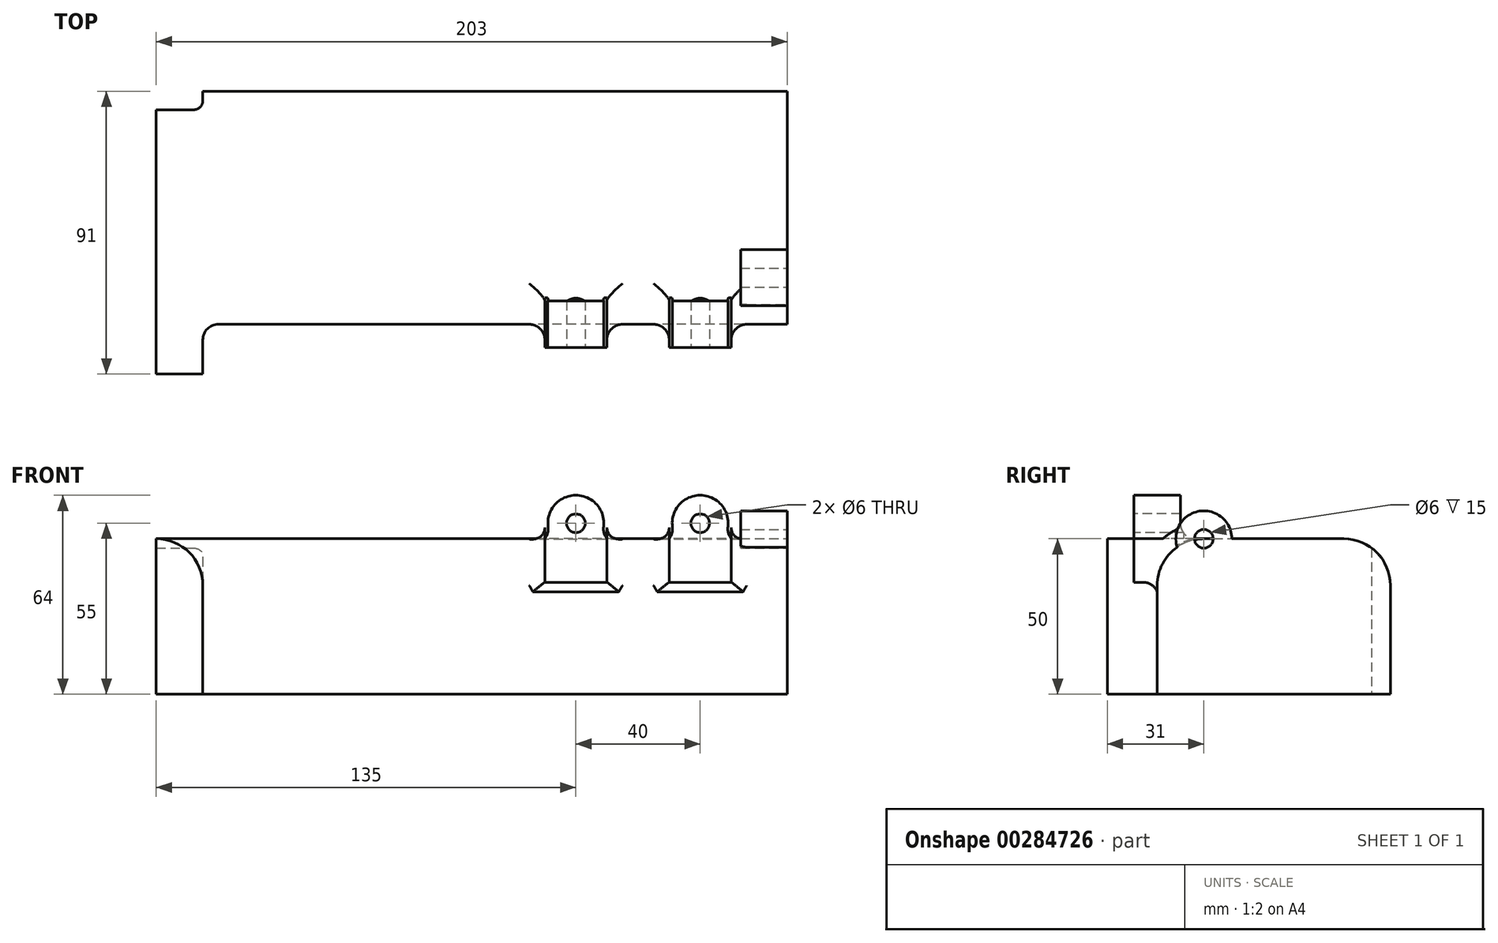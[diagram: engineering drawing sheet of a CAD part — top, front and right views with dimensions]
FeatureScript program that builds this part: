
annotation { "Feature Type Name" : "Feature", "Feature Type Description" : "" }
export const myFeature = defineFeature(function(context is Context, id is Id, definition is map)
    precondition{}
    {
        {
            var Q0;
            Q0=qCreatedBy(makeId("Top.planeOp"),FACE);
            var sketch = newSketch(context, id + "F0", { "sketchPlane" : qUnion([Q0])});
            skLineSegment(sketch, "E0.bottom", {"start": v(4.5, 42.5) * mm, "end": v(-7.5, 42.5) * mm});
            skLineSegment(sketch, "E0.top", {"start": v(7.5, -42.5) * mm, "end": v(-7.5, -42.5) * mm});
            skLineSegment(sketch, "E0.left", {"start": v(7.5, -31.5) * mm, "end": v(7.5, -42.5) * mm});
            skLineSegment(sketch, "E0.right", {"start": v(-7.5, 42.5) * mm, "end": v(-7.5, -42.5) * mm});
            skPoint(sketch, "E0.middle", {"position": v(0, 0) * mm});
            skLineSegment(sketch, "E1", {"start": v(7.5, 45.5) * mm, "end": v(7.5, 48.5) * mm});
            skLineSegment(sketch, "E2", {"start": v(7.5, 48.5) * mm, "end": v(195.5, 48.5) * mm});
            skLineSegment(sketch, "E3", {"start": v(195.5, 48.5) * mm, "end": v(195.5, -26.5) * mm});
            skLineSegment(sketch, "E4", {"start": v(195.5, -26.5) * mm, "end": v(12.5, -26.5) * mm});
            skPoint(sketch, "E5.visualSharp", {"position": v(7.5, 42.5) * mm});
            skArc(sketch, "E5.filletArc", {"start": v(4.5, 42.5) * mm, "mid": v(6.62, 43.38) * mm, "end": v(7.5, 45.5) * mm});
            skArc(sketch, "E6.filletArc", {"start": v(12.5, -26.5) * mm, "mid": v(8.96, -27.96) * mm, "end": v(7.5, -31.5) * mm});
            skSolve(sketch);
        }
        {
            var Q0;
            Q0=qSketchRegion(id+"F0",true);
            extrude(context, id + "F1", {"entities" : qUnion([Q0]), "depth" : 50 * mm});
        }
        {
            var Q0;
            Q0=makeQuery(id+"F1.opExtrude","CAP_EDGE",EDGE,{"disambiguationData":[OSD([sQuery(id+"F0.wireOp",EDGE,"E4")])],"isStart":false});
            var Q1;
            Q1=makeQuery(id+"F1.opExtrude","CAP_EDGE",EDGE,{"disambiguationData":[OSD([sQuery(id+"F0.wireOp",EDGE,"E2")])],"isStart":false});
            fillet(context, id + "F2", {"entities" : qUnion([Q0, Q1]), "radius" : 15 * mm, "tangentPropagation" : true, "allowEdgeOverflow" : false});
        }
        {
            var Q0;
            Q0=makeQuery(id+"F1.opExtrude","CAP_FACE",FACE,{"disambiguationData":[OSD([sQuery(id+"F0.wireOp",EDGE,"E0.bottom"),sQuery(id+"F0.wireOp",EDGE,"E0.top"),sQuery(id+"F0.wireOp",EDGE,"E0.left"),sQuery(id+"F0.wireOp",EDGE,"E0.right"),sQuery(id+"F0.wireOp",EDGE,"E1"),sQuery(id+"F0.wireOp",EDGE,"E2"),sQuery(id+"F0.wireOp",EDGE,"E3"),sQuery(id+"F0.wireOp",EDGE,"E4"),sQuery(id+"F0.wireOp",EDGE,"E5.filletArc"),sQuery(id+"F0.wireOp",EDGE,"E6.filletArc")])],"isStart":false});
            var sketch = newSketch(context, id + "F3", { "sketchPlane" : qUnion([Q0])});
            skLineSegment(sketch, "E7.0.0", {"start": v(195.5, 48.5) * mm, "end": v(180.5, 33.5) * mm, "construction": true});
            skLineSegment(sketch, "E7.0.1", {"start": v(180.5, -11.5) * mm, "end": v(180.5, 33.5) * mm, "construction": true});
            skLineSegment(sketch, "E7.0.2", {"start": v(180.5, -11.5) * mm, "end": v(195.5, -26.5) * mm, "construction": true});
            skLineSegment(sketch, "E7.0.3", {"start": v(195.5, -26.5) * mm, "end": v(195.5, 48.5) * mm, "construction": true});
            skLineSegment(sketch, "E8.0", {"start": v(195.5, -26.5) * mm, "end": v(12.5, -26.5) * mm, "construction": true});
            skLineSegment(sketch, "E9.0", {"start": v(12.5, -11.5) * mm, "end": v(180.5, -11.5) * mm, "construction": true});
            skPoint(sketch, "E10", {"position": v(167.5, -26.5) * mm});
            skPoint(sketch, "E11", {"position": v(127.5, -26.5) * mm});
            skLineSegment(sketch, "E12.bottom", {"start": v(177.5, -19) * mm, "end": v(157.5, -19) * mm});
            skLineSegment(sketch, "E12.top", {"start": v(177.5, -34) * mm, "end": v(157.5, -34) * mm});
            skLineSegment(sketch, "E12.left", {"start": v(177.5, -19) * mm, "end": v(177.5, -34) * mm});
            skLineSegment(sketch, "E12.right", {"start": v(157.5, -19) * mm, "end": v(157.5, -34) * mm});
            skLineSegment(sketch, "E13.bottom", {"start": v(137.5, -19) * mm, "end": v(117.5, -19) * mm});
            skLineSegment(sketch, "E13.top", {"start": v(137.5, -34) * mm, "end": v(117.5, -34) * mm});
            skLineSegment(sketch, "E13.left", {"start": v(137.5, -19) * mm, "end": v(137.5, -34) * mm});
            skLineSegment(sketch, "E13.right", {"start": v(117.5, -19) * mm, "end": v(117.5, -34) * mm});
            skSolve(sketch);
        }
        {
            var Q0;
            Q0=qSketchRegion(id+"F3",true);
            extrude(context, id + "F4", {"entities" : qUnion([Q0]), "operationType" : NewBodyOperationType.ADD, "endBound" : BoundingType.SYMMETRIC, "depth" : 28 * mm});
        }
        {
            var Q0;
            Q0=makeQuery(id+"F4.boolean.opBoolean","INTERSECT",EDGE,{"derivedFrom":[makeQuery(id+"F2.opFillet","BLEND_FACE",FACE,{"disambiguationData":[OSD([sQuery(id+"F0.wireOp",EDGE,"E4")])]}),makeQuery(id+"F4.opExtrude","SWEPT_FACE",FACE,{"disambiguationData":[OSD([sQuery(id+"F3.wireOp",EDGE,"E13.bottom")])]})]});
            var Q1;
            Q1=makeQuery(id+"F4.boolean.opBoolean","INTERSECT",EDGE,{"derivedFrom":[makeQuery(id+"F2.opFillet","BLEND_FACE",FACE,{"disambiguationData":[OSD([sQuery(id+"F0.wireOp",EDGE,"E4")])]}),makeQuery(id+"F4.opExtrude","SWEPT_FACE",FACE,{"disambiguationData":[OSD([sQuery(id+"F3.wireOp",EDGE,"E12.bottom")])]})]});
            var Q2;
            Q2=makeQuery(id+"F4.boolean.opBoolean","INTERSECT",EDGE,{"derivedFrom":[makeQuery(id+"F2.opFillet","BLEND_FACE",FACE,{"disambiguationData":[OSD([sQuery(id+"F0.wireOp",EDGE,"E4")])]}),makeQuery(id+"F4.opExtrude","SWEPT_FACE",FACE,{"disambiguationData":[OSD([sQuery(id+"F3.wireOp",EDGE,"E12.left")])]})]});
            var Q3;
            Q3=makeQuery(id+"F4.boolean.opBoolean","INTERSECT",EDGE,{"derivedFrom":[makeQuery(id+"F2.opFillet","BLEND_FACE",FACE,{"disambiguationData":[OSD([sQuery(id+"F0.wireOp",EDGE,"E4")])]}),makeQuery(id+"F4.opExtrude","SWEPT_FACE",FACE,{"disambiguationData":[OSD([sQuery(id+"F3.wireOp",EDGE,"E12.right")])]})]});
            var Q4;
            Q4=makeQuery(id+"F4.boolean.opBoolean","INTERSECT",EDGE,{"derivedFrom":[makeQuery(id+"F2.opFillet","BLEND_FACE",FACE,{"disambiguationData":[OSD([sQuery(id+"F0.wireOp",EDGE,"E4")])]}),makeQuery(id+"F4.opExtrude","CAP_FACE",FACE,{"disambiguationData":[OSD([sQuery(id+"F3.wireOp",EDGE,"E12.bottom"),sQuery(id+"F3.wireOp",EDGE,"E12.top"),sQuery(id+"F3.wireOp",EDGE,"E12.left"),sQuery(id+"F3.wireOp",EDGE,"E12.right")])],"isStart":true})]});
            var Q5;
            Q5=makeQuery(id+"F4.boolean.opBoolean","INTERSECT",EDGE,{"derivedFrom":[makeQuery(id+"F2.opFillet","BLEND_FACE",FACE,{"disambiguationData":[OSD([sQuery(id+"F0.wireOp",EDGE,"E4")])]}),makeQuery(id+"F4.opExtrude","SWEPT_FACE",FACE,{"disambiguationData":[OSD([sQuery(id+"F3.wireOp",EDGE,"E13.right")])]})]});
            var Q6;
            Q6=makeQuery(id+"F4.boolean.opBoolean","INTERSECT",EDGE,{"derivedFrom":[makeQuery(id+"F2.opFillet","BLEND_FACE",FACE,{"disambiguationData":[OSD([sQuery(id+"F0.wireOp",EDGE,"E4")])]}),makeQuery(id+"F4.opExtrude","CAP_FACE",FACE,{"disambiguationData":[OSD([sQuery(id+"F3.wireOp",EDGE,"E13.bottom"),sQuery(id+"F3.wireOp",EDGE,"E13.top"),sQuery(id+"F3.wireOp",EDGE,"E13.left"),sQuery(id+"F3.wireOp",EDGE,"E13.right")])],"isStart":true})]});
            var Q7;
            Q7=makeQuery(id+"F4.boolean.opBoolean","INTERSECT",EDGE,{"derivedFrom":[makeQuery(id+"F2.opFillet","BLEND_FACE",FACE,{"disambiguationData":[OSD([sQuery(id+"F0.wireOp",EDGE,"E4")])]}),makeQuery(id+"F4.opExtrude","SWEPT_FACE",FACE,{"disambiguationData":[OSD([sQuery(id+"F3.wireOp",EDGE,"E13.left")])]})]});
            fillet(context, id + "F5", {"entities" : qUnion([Q0, Q1, Q2, Q3, Q4, Q5, Q6, Q7]), "radius" : 5 * mm, "tangentPropagation" : true, "allowEdgeOverflow" : false});
        }
        {
            var Q0;
            Q0=makeQuery(id+"F4.opExtrude","SWEPT_FACE",FACE,{"disambiguationData":[OSD([sQuery(id+"F3.wireOp",EDGE,"E12.top")])]});
            var sketch = newSketch(context, id + "F6", { "sketchPlane" : qUnion([Q0])});
            skLineSegment(sketch, "E14.0", {"start": v(137.5, 64) * mm, "end": v(137.5, 36) * mm});
            skLineSegment(sketch, "E15.0", {"start": v(137.5, 64) * mm, "end": v(117.5, 64) * mm});
            skLineSegment(sketch, "E16.0", {"start": v(117.5, 64) * mm, "end": v(117.5, 36) * mm});
            skLineSegment(sketch, "E17.0", {"start": v(137.5, 36) * mm, "end": v(117.5, 36) * mm});
            skLineSegment(sketch, "E18.0", {"start": v(177.5, 64) * mm, "end": v(157.5, 64) * mm});
            skLineSegment(sketch, "E19.0", {"start": v(177.5, 64) * mm, "end": v(177.5, 36) * mm});
            skLineSegment(sketch, "E20.0", {"start": v(157.5, 64) * mm, "end": v(157.5, 36) * mm});
            skLineSegment(sketch, "E21.0", {"start": v(177.5, 36) * mm, "end": v(157.5, 36) * mm});
            skPoint(sketch, "E22", {"position": v(167.5, 55) * mm});
            skPoint(sketch, "E22.positionSnap0", {"position": v(167.5, 64) * mm});
            skCircle(sketch, "E23", {"center": v(167.5, 55) * mm, "radius": 9 * mm});
            skCircle(sketch, "E24", {"center": v(167.5, 55) * mm, "radius": 3 * mm});
            skPoint(sketch, "E25", {"position": v(127.5, 55) * mm});
            skPoint(sketch, "E25.positionSnap0", {"position": v(127.5, 64) * mm});
            skCircle(sketch, "E26", {"center": v(127.5, 55) * mm, "radius": 9 * mm});
            skCircle(sketch, "E27", {"center": v(127.5, 55) * mm, "radius": 3 * mm});
            skLineSegment(sketch, "E28", {"start": v(157.5, 50) * mm, "end": v(160.02, 50) * mm});
            skLineSegment(sketch, "E29", {"start": v(177.5, 50) * mm, "end": v(174.98, 50) * mm});
            skLineSegment(sketch, "E30", {"start": v(117.5, 50) * mm, "end": v(120.02, 50) * mm});
            skLineSegment(sketch, "E31", {"start": v(137.5, 50) * mm, "end": v(134.98, 50) * mm});
            skLineSegment(sketch, "E32", {"start": v(117.5, 64) * mm, "end": v(137.5, 64) * mm});
            skLineSegment(sketch, "E33", {"start": v(157.5, 64) * mm, "end": v(177.5, 64) * mm});
            skSolve(sketch);
        }
        {
            var Q0;
            {var subQ3=sQuery(id+"F6.wireOp",EDGE,"E31");Q0=makeQuery(id+"F6.imprint","IMPRINT",FACE,{"disambiguationData":[TD([[makeQuery(id+"F6.imprint","IMPRINT",EDGE,{"derivedFrom":subQ3}),-1.0]])]});}
            var Q1;
            {var subQ3=sQuery(id+"F6.wireOp",EDGE,"E30");Q1=makeQuery(id+"F6.imprint","IMPRINT",FACE,{"disambiguationData":[TD([[makeQuery(id+"F6.imprint","IMPRINT",EDGE,{"derivedFrom":subQ3}),1.0]])]});}
            var Q2;
            {var subQ3=sQuery(id+"F6.wireOp",EDGE,"E29");Q2=makeQuery(id+"F6.imprint","IMPRINT",FACE,{"disambiguationData":[TD([[makeQuery(id+"F6.imprint","IMPRINT",EDGE,{"derivedFrom":subQ3}),-1.0]])]});}
            var Q3;
            {var subQ3=sQuery(id+"F6.wireOp",EDGE,"E28");Q3=makeQuery(id+"F6.imprint","IMPRINT",FACE,{"disambiguationData":[TD([[makeQuery(id+"F6.imprint","IMPRINT",EDGE,{"derivedFrom":subQ3}),1.0]])]});}
            var Q4;
            Q4=makeQuery(id+"F6.imprint","IMPRINT",FACE,{"disambiguationData":[TD([[makeQuery(id+"F6.imprint","IMPRINT",EDGE,{"derivedFrom":sQuery(id+"F6.wireOp",EDGE,"E24")}),1.0]])]});
            var Q5;
            Q5=makeQuery(id+"F6.imprint","IMPRINT",FACE,{"disambiguationData":[TD([[makeQuery(id+"F6.imprint","IMPRINT",EDGE,{"derivedFrom":sQuery(id+"F6.wireOp",EDGE,"E27")}),1.0]])]});
            extrude(context, id + "F7", {"entities" : qUnion([Q0, Q1, Q2, Q3, Q4, Q5]), "operationType" : NewBodyOperationType.REMOVE, "oppositeDirection" : true, "depth" : 16 * mm});
        }
        {
            var Q0;
            Q0=makeQuery(id+"F7.boolean.opBoolean","COPY",EDGE,{"derivedFrom":makeQuery(id+"F7.opExtrude","SWEPT_EDGE",EDGE,{"disambiguationData":[OSD([sQuery(id+"F6.wireOp",EDGE,"E23"),sQuery(id+"F6.wireOp",EDGE,"E28")])]})});
            var Q1;
            Q1=makeQuery(id+"F7.boolean.opBoolean","COPY",EDGE,{"derivedFrom":makeQuery(id+"F7.opExtrude","SWEPT_EDGE",EDGE,{"disambiguationData":[OSD([sQuery(id+"F6.wireOp",EDGE,"E23"),sQuery(id+"F6.wireOp",EDGE,"E29")])]})});
            var Q2;
            Q2=makeQuery(id+"F7.boolean.opBoolean","COPY",EDGE,{"derivedFrom":makeQuery(id+"F7.opExtrude","SWEPT_EDGE",EDGE,{"disambiguationData":[OSD([sQuery(id+"F6.wireOp",EDGE,"E26"),sQuery(id+"F6.wireOp",EDGE,"E31")])]})});
            var Q3;
            Q3=makeQuery(id+"F7.boolean.opBoolean","COPY",EDGE,{"derivedFrom":makeQuery(id+"F7.opExtrude","SWEPT_EDGE",EDGE,{"disambiguationData":[OSD([sQuery(id+"F6.wireOp",EDGE,"E26"),sQuery(id+"F6.wireOp",EDGE,"E30")])]})});
            fillet(context, id + "F8", {"entities" : qUnion([Q0, Q1, Q2, Q3]), "radius" : 5 * mm, "tangentPropagation" : true, "allowEdgeOverflow" : false});
        }
        {
            var Q0;
            Q0=makeQuery(id+"F1.opExtrude","SWEPT_FACE",FACE,{"disambiguationData":[OSD([sQuery(id+"F0.wireOp",EDGE,"E3")])]});
            var sketch = newSketch(context, id + "F9", { "sketchPlane" : qUnion([Q0])});
            skLineSegment(sketch, "E34.0", {"start": v(33.5, 50) * mm, "end": v(-11.5, 50) * mm});
            skCircle(sketch, "E35", {"center": v(-11.5, 50) * mm, "radius": 3 * mm});
            skCircle(sketch, "E36", {"center": v(-11.5, 50) * mm, "radius": 9 * mm});
            skPoint(sketch, "E37", {"position": v(-20.5, 50) * mm});
            skLineSegment(sketch, "E38", {"start": v(-20.5, 50) * mm, "end": v(-22.1, 45.6) * mm});
            skSolve(sketch);
        }
        {
            var Q0;
            Q0=qSketchRegion(id+"F9",true);
            extrude(context, id + "F10", {"entities" : qUnion([Q0]), "operationType" : NewBodyOperationType.ADD, "oppositeDirection" : true, "depth" : 15 * mm});
        }
        {
            var Q0;
            Q0=makeQuery(id+"F10.boolean.opBoolean","MERGE",FACE,{"derivedFrom":[makeQuery(id+"F1.opExtrude","SWEPT_FACE",FACE,{"disambiguationData":[OSD([sQuery(id+"F0.wireOp",EDGE,"E3")])]}),makeQuery(id+"F10.opExtrude","CAP_FACE",FACE,{"disambiguationData":[OSD([sQuery(id+"F9.wireOp",EDGE,"E35"),sQuery(id+"F9.wireOp",EDGE,"E36")])],"isStart":true})]});
            var sketch = newSketch(context, id + "F11", { "sketchPlane" : qUnion([Q0])});
            skArc(sketch, "E39.0", {"start": v(-8.5, 50) * mm, "mid": v(-11.65, 53) * mm, "end": v(-14.48, 49.7) * mm});
            skCircle(sketch, "E40", {"center": v(-11.5, 50) * mm, "radius": 3 * mm});
            skSolve(sketch);
        }
        {
            var Q0;
            Q0=qSketchRegion(id+"F11",true);
            extrude(context, id + "F12", {"entities" : qUnion([Q0]), "operationType" : NewBodyOperationType.REMOVE, "oppositeDirection" : true, "depth" : 15 * mm});
        }
    });
